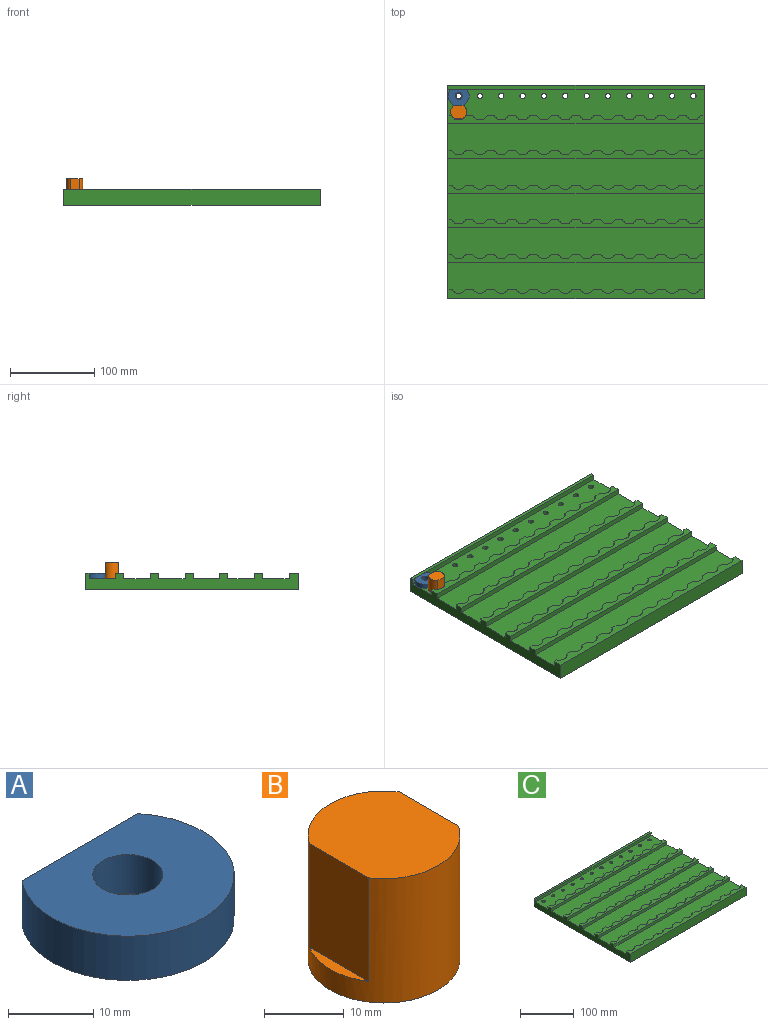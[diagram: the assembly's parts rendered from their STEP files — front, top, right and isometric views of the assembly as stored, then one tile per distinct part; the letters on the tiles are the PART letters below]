
ASSEMBLY  parts=3 mates=1
PART A: 7 faces, bbox 24.9x20.4x6.4 mm
  f0: plane 24.89x20.37mm, normal (0,0,-1), area 379.2mm2, adj f1,f2,f3
  f1: cylinder r=3.87mm len=7.75mm, axis (0,0,1), area 18.5mm2, adj f0,f4
  f2: cylinder r=12.45mm len=24.89mm, axis (0,0,-1), area 357.4mm2, adj f0,f3,f5
  f3: plane 19.19x6.35mm, normal (0,1,0), area 121.9mm2, adj f0,f2,f5
  f4: plane 8.2x8.2mm, normal (0,0,1), area 5.7mm2, adj f1,f6
  f5: plane 24.89x20.37mm, normal (0,0,1), area 373.4mm2, adj f2,f3,f6
  f6: cylinder r=4.1mm len=8.2mm, axis (0,0,1), area 144mm2, adj f4,f5
PART B: 7 faces, bbox 19.1x19.1x19.1 mm
  f0: cylinder r=9.53mm len=19.05mm, axis (0,0,-1), area 785.8mm2, adj f1,f2,f3,f4,f5,f6
  f1: plane 19.05x15.88mm, normal (0,0,1), area 262.3mm2, adj f0,f4,f6
  f2: plane 19.05x19.05mm, normal (0,0,-1), area 285mm2, adj f0
  f3: plane 10.53x1.59mm, normal (0,0,1), area 11.3mm2, adj f0,f4
  f4: plane 15.88x10.53mm, normal (1,0,0), area 167.2mm2, adj f0,f1,f3
  f5: plane 10.53x1.59mm, normal (0,0,1), area 11.3mm2, adj f0,f6
  f6: plane 15.88x10.53mm, normal (-1,0,0), area 167.2mm2, adj f0,f1,f5
PART C: 186 faces, bbox 304.8x254x19.1 mm
  f0: plane 254x19.05mm, normal (-1,0,0), area 3629mm2, adj f1,f2,f3,f4,f5,f6,f19,f20
  f1: plane 304.8x9.53mm, normal (0,0,1), area 2171mm2, adj f0,f21,f132,f133,f134,f135,f136,f137
  f2: plane 304.8x9.53mm, normal (0,0,1), area 2171mm2, adj f0,f21,f105,f106,f107,f108,f109,f110
  f3: plane 304.8x9.53mm, normal (0,0,1), area 2171mm2, adj f0,f21,f78,f79,f80,f81,f82,f83
  f4: plane 304.8x9.53mm, normal (0,0,1), area 2171mm2, adj f0,f21,f51,f52,f53,f54,f55,f56
  f5: plane 304.8x9.53mm, normal (0,0,1), area 2171mm2, adj f0,f21,f25,f26,f27,f28,f29,f30
  f6: plane 304.8x4.45mm, normal (0,0,1), area 1354.8mm2, adj f0,f19,f21,f45
  f7: cylinder r=3.17mm len=12.7mm, axis (0,0,1), area 253.4mm2, adj f22,f24
  f8: cylinder r=3.17mm len=12.7mm, axis (0,0,1), area 253.4mm2, adj f22,f24
  f9: cylinder r=3.17mm len=12.7mm, axis (0,0,1), area 253.4mm2, adj f22,f24
  f10: cylinder r=3.17mm len=12.7mm, axis (0,0,1), area 253.4mm2, adj f22,f24
  f11: cylinder r=3.17mm len=12.7mm, axis (0,0,1), area 253.4mm2, adj f22,f24
  f12: cylinder r=3.17mm len=12.7mm, axis (0,0,1), area 253.4mm2, adj f22,f24
  f13: cylinder r=3.17mm len=12.7mm, axis (0,0,1), area 253.4mm2, adj f22,f24
  f14: cylinder r=3.17mm len=12.7mm, axis (0,0,1), area 253.4mm2, adj f22,f24
  f15: cylinder r=3.17mm len=12.7mm, axis (0,0,1), area 253.4mm2, adj f22,f24
  f16: cylinder r=3.17mm len=12.7mm, axis (0,0,1), area 253.4mm2, adj f22,f24
  f17: cylinder r=3.17mm len=12.7mm, axis (0,0,1), area 253.4mm2, adj f22,f24
  f18: cylinder r=3.17mm len=12.7mm, axis (0,0,1), area 253.4mm2, adj f22,f24
  f19: plane 304.8x19.05mm, normal (0,1,0), area 5806.4mm2, adj f0,f6,f21,f22
  f20: plane 304.8x19.05mm, normal (0,-1,0), area 5806.4mm2, adj f0,f21,f22,f23
  f21: plane 254x19.05mm, normal (1,0,0), area 3629mm2, adj f1,f2,f3,f4,f5,f6,f19,f20
  f22: plane 304.8x254mm, normal (0,0,-1), area 77039.2mm2, adj f0,f7,f8,f9,f10,f11,f12,f13
  f23: plane 304.8x11.43mm, normal (0,0,1), area 2751.7mm2, adj f0,f20,f21,f159,f160,f161,f162,f163
  f24: plane 304.8x36.83mm, normal (0,0,1), area 10029.6mm2, adj f0,f7,f8,f9,f10,f11,f12,f13
  f25: cylinder r=9.53mm len=16.85mm, axis (0,0,1), area 131.3mm2, adj f5,f24,f26,f50
  f26: plane 8.55x6.35mm, normal (0,1,0), area 54.3mm2, adj f5,f24,f25,f27
  f27: cylinder r=9.53mm len=16.85mm, axis (0,0,1), area 131.3mm2, adj f5,f24,f26,f28
  f28: plane 8.55x6.35mm, normal (0,1,0), area 54.3mm2, adj f5,f24,f27,f29
  f29: cylinder r=9.53mm len=16.85mm, axis (0,0,1), area 131.3mm2, adj f5,f24,f28,f30
  f30: plane 8.55x6.35mm, normal (0,1,0), area 54.3mm2, adj f5,f24,f29,f31
  f31: cylinder r=9.53mm len=16.85mm, axis (0,0,1), area 131.3mm2, adj f5,f24,f30,f32
  f32: plane 8.55x6.35mm, normal (0,1,0), area 54.3mm2, adj f5,f24,f31,f33
  f33: cylinder r=9.53mm len=16.85mm, axis (0,0,1), area 131.3mm2, adj f5,f24,f32,f34
  f34: plane 8.55x6.35mm, normal (0,1,0), area 54.3mm2, adj f5,f24,f33,f35
  f35: cylinder r=9.53mm len=16.85mm, axis (0,0,1), area 131.3mm2, adj f5,f24,f34,f36
  f36: plane 8.55x6.35mm, normal (0,1,0), area 54.3mm2, adj f5,f24,f35,f37
  f37: cylinder r=9.53mm len=16.85mm, axis (0,0,1), area 131.3mm2, adj f5,f24,f36,f38
  f38: plane 8.55x6.35mm, normal (0,1,0), area 54.3mm2, adj f5,f24,f37,f39
  f39: cylinder r=9.53mm len=16.85mm, axis (0,0,1), area 131.3mm2, adj f5,f24,f38,f40
  f40: plane 8.55x6.35mm, normal (0,1,0), area 54.3mm2, adj f5,f24,f39,f41
  f41: cylinder r=9.53mm len=16.85mm, axis (0,0,1), area 131.3mm2, adj f5,f24,f40,f42
  f42: plane 8.55x6.35mm, normal (0,1,0), area 54.3mm2, adj f5,f24,f41,f43
  f43: cylinder r=9.53mm len=16.85mm, axis (0,0,1), area 131.3mm2, adj f5,f24,f42,f44
  f44: plane 6.35x4.28mm, normal (0,1,0), area 27.2mm2, adj f5,f21,f24,f43
  f45: plane 304.8x6.35mm, normal (0,-1,0), area 1935.5mm2, adj f0,f6,f21,f24
  f46: plane 6.35x4.28mm, normal (0,1,0), area 27.2mm2, adj f0,f5,f24,f47
  f47: cylinder r=9.53mm len=16.85mm, axis (0,0,1), area 131.3mm2, adj f5,f24,f46,f48
  f48: plane 8.55x6.35mm, normal (0,1,0), area 54.3mm2, adj f5,f24,f47,f49
  f49: cylinder r=9.53mm len=16.85mm, axis (0,0,1), area 131.3mm2, adj f5,f24,f48,f50
  f50: plane 8.55x6.35mm, normal (0,1,0), area 54.3mm2, adj f5,f24,f25,f49
  f51: cylinder r=9.53mm len=16.85mm, axis (0,0,1), area 131.3mm2, adj f4,f52,f76,f77
  f52: plane 8.55x6.35mm, normal (0,1,0), area 54.3mm2, adj f4,f51,f53,f77
  f53: cylinder r=9.53mm len=16.85mm, axis (0,0,1), area 131.3mm2, adj f4,f52,f54,f77
  f54: plane 8.55x6.35mm, normal (0,1,0), area 54.3mm2, adj f4,f53,f55,f77
  f55: cylinder r=9.53mm len=16.85mm, axis (0,0,1), area 131.3mm2, adj f4,f54,f56,f77
  f56: plane 8.55x6.35mm, normal (0,1,0), area 54.3mm2, adj f4,f55,f57,f77
  f57: cylinder r=9.53mm len=16.85mm, axis (0,0,1), area 131.3mm2, adj f4,f56,f58,f77
  f58: plane 8.55x6.35mm, normal (0,1,0), area 54.3mm2, adj f4,f57,f59,f77
  f59: cylinder r=9.53mm len=16.85mm, axis (0,0,1), area 131.3mm2, adj f4,f58,f60,f77
  f60: plane 8.55x6.35mm, normal (0,1,0), area 54.3mm2, adj f4,f59,f61,f77
  f61: cylinder r=9.53mm len=16.85mm, axis (0,0,1), area 131.3mm2, adj f4,f60,f62,f77
  f62: plane 8.55x6.35mm, normal (0,1,0), area 54.3mm2, adj f4,f61,f63,f77
  f63: cylinder r=9.53mm len=16.85mm, axis (0,0,1), area 131.3mm2, adj f4,f62,f64,f77
  f64: plane 8.55x6.35mm, normal (0,1,0), area 54.3mm2, adj f4,f63,f65,f77
  f65: cylinder r=9.53mm len=16.85mm, axis (0,0,1), area 131.3mm2, adj f4,f64,f66,f77
  f66: plane 8.55x6.35mm, normal (0,1,0), area 54.3mm2, adj f4,f65,f67,f77
  f67: cylinder r=9.53mm len=16.85mm, axis (0,0,1), area 131.3mm2, adj f4,f66,f68,f77
  f68: plane 8.55x6.35mm, normal (0,1,0), area 54.3mm2, adj f4,f67,f69,f77
  f69: cylinder r=9.53mm len=16.85mm, axis (0,0,1), area 131.3mm2, adj f4,f68,f70,f77
  f70: plane 6.35x4.28mm, normal (0,1,0), area 27.2mm2, adj f4,f21,f69,f77
  f71: plane 304.8x6.35mm, normal (0,-1,0), area 1935.5mm2, adj f0,f5,f21,f77
  f72: plane 6.35x4.28mm, normal (0,1,0), area 27.2mm2, adj f0,f4,f73,f77
  f73: cylinder r=9.53mm len=16.85mm, axis (0,0,1), area 131.3mm2, adj f4,f72,f74,f77
  f74: plane 8.55x6.35mm, normal (0,1,0), area 54.3mm2, adj f4,f73,f75,f77
  f75: cylinder r=9.53mm len=16.85mm, axis (0,0,1), area 131.3mm2, adj f4,f74,f76,f77
  f76: plane 8.55x6.35mm, normal (0,1,0), area 54.3mm2, adj f4,f51,f75,f77
  f77: plane 304.8x36.83mm, normal (0,0,1), area 10409.6mm2, adj f0,f21,f51,f52,f53,f54,f55,f56
  f78: cylinder r=9.53mm len=16.85mm, axis (0,0,1), area 131.3mm2, adj f3,f79,f103,f104
  f79: plane 8.55x6.35mm, normal (0,1,0), area 54.3mm2, adj f3,f78,f80,f104
  f80: cylinder r=9.53mm len=16.85mm, axis (0,0,1), area 131.3mm2, adj f3,f79,f81,f104
  f81: plane 8.55x6.35mm, normal (0,1,0), area 54.3mm2, adj f3,f80,f82,f104
  f82: cylinder r=9.53mm len=16.85mm, axis (0,0,1), area 131.3mm2, adj f3,f81,f83,f104
  f83: plane 8.55x6.35mm, normal (0,1,0), area 54.3mm2, adj f3,f82,f84,f104
  f84: cylinder r=9.53mm len=16.85mm, axis (0,0,1), area 131.3mm2, adj f3,f83,f85,f104
  f85: plane 8.55x6.35mm, normal (0,1,0), area 54.3mm2, adj f3,f84,f86,f104
  f86: cylinder r=9.53mm len=16.85mm, axis (0,0,1), area 131.3mm2, adj f3,f85,f87,f104
  f87: plane 8.55x6.35mm, normal (0,1,0), area 54.3mm2, adj f3,f86,f88,f104
  f88: cylinder r=9.53mm len=16.85mm, axis (0,0,1), area 131.3mm2, adj f3,f87,f89,f104
  f89: plane 8.55x6.35mm, normal (0,1,0), area 54.3mm2, adj f3,f88,f90,f104
  f90: cylinder r=9.53mm len=16.85mm, axis (0,0,1), area 131.3mm2, adj f3,f89,f91,f104
  f91: plane 8.55x6.35mm, normal (0,1,0), area 54.3mm2, adj f3,f90,f92,f104
  f92: cylinder r=9.53mm len=16.85mm, axis (0,0,1), area 131.3mm2, adj f3,f91,f93,f104
  f93: plane 8.55x6.35mm, normal (0,1,0), area 54.3mm2, adj f3,f92,f94,f104
  f94: cylinder r=9.53mm len=16.85mm, axis (0,0,1), area 131.3mm2, adj f3,f93,f95,f104
  f95: plane 8.55x6.35mm, normal (0,1,0), area 54.3mm2, adj f3,f94,f96,f104
  f96: cylinder r=9.53mm len=16.85mm, axis (0,0,1), area 131.3mm2, adj f3,f95,f97,f104
  f97: plane 6.35x4.28mm, normal (0,1,0), area 27.2mm2, adj f3,f21,f96,f104
  f98: plane 304.8x6.35mm, normal (0,-1,0), area 1935.5mm2, adj f0,f4,f21,f104
  f99: plane 6.35x4.28mm, normal (0,1,0), area 27.2mm2, adj f0,f3,f100,f104
  f100: cylinder r=9.53mm len=16.85mm, axis (0,0,1), area 131.3mm2, adj f3,f99,f101,f104
  f101: plane 8.55x6.35mm, normal (0,1,0), area 54.3mm2, adj f3,f100,f102,f104
  f102: cylinder r=9.53mm len=16.85mm, axis (0,0,1), area 131.3mm2, adj f3,f101,f103,f104
  f103: plane 8.55x6.35mm, normal (0,1,0), area 54.3mm2, adj f3,f78,f102,f104
  f104: plane 304.8x36.83mm, normal (0,0,1), area 10409.6mm2, adj f0,f21,f78,f79,f80,f81,f82,f83
  f105: cylinder r=9.53mm len=16.85mm, axis (0,0,1), area 131.3mm2, adj f2,f106,f130,f131
  f106: plane 8.55x6.35mm, normal (0,1,0), area 54.3mm2, adj f2,f105,f107,f131
  f107: cylinder r=9.53mm len=16.85mm, axis (0,0,1), area 131.3mm2, adj f2,f106,f108,f131
  f108: plane 8.55x6.35mm, normal (0,1,0), area 54.3mm2, adj f2,f107,f109,f131
  f109: cylinder r=9.53mm len=16.85mm, axis (0,0,1), area 131.3mm2, adj f2,f108,f110,f131
  f110: plane 8.55x6.35mm, normal (0,1,0), area 54.3mm2, adj f2,f109,f111,f131
  f111: cylinder r=9.53mm len=16.85mm, axis (0,0,1), area 131.3mm2, adj f2,f110,f112,f131
  f112: plane 8.55x6.35mm, normal (0,1,0), area 54.3mm2, adj f2,f111,f113,f131
  f113: cylinder r=9.53mm len=16.85mm, axis (0,0,1), area 131.3mm2, adj f2,f112,f114,f131
  f114: plane 8.55x6.35mm, normal (0,1,0), area 54.3mm2, adj f2,f113,f115,f131
  f115: cylinder r=9.53mm len=16.85mm, axis (0,0,1), area 131.3mm2, adj f2,f114,f116,f131
  f116: plane 8.55x6.35mm, normal (0,1,0), area 54.3mm2, adj f2,f115,f117,f131
  f117: cylinder r=9.53mm len=16.85mm, axis (0,0,1), area 131.3mm2, adj f2,f116,f118,f131
  f118: plane 8.55x6.35mm, normal (0,1,0), area 54.3mm2, adj f2,f117,f119,f131
  f119: cylinder r=9.53mm len=16.85mm, axis (0,0,1), area 131.3mm2, adj f2,f118,f120,f131
  f120: plane 8.55x6.35mm, normal (0,1,0), area 54.3mm2, adj f2,f119,f121,f131
  f121: cylinder r=9.53mm len=16.85mm, axis (0,0,1), area 131.3mm2, adj f2,f120,f122,f131
  f122: plane 8.55x6.35mm, normal (0,1,0), area 54.3mm2, adj f2,f121,f123,f131
  f123: cylinder r=9.53mm len=16.85mm, axis (0,0,1), area 131.3mm2, adj f2,f122,f124,f131
  f124: plane 6.35x4.28mm, normal (0,1,0), area 27.2mm2, adj f2,f21,f123,f131
  f125: plane 304.8x6.35mm, normal (0,-1,0), area 1935.5mm2, adj f0,f3,f21,f131
  f126: plane 6.35x4.28mm, normal (0,1,0), area 27.2mm2, adj f0,f2,f127,f131
  f127: cylinder r=9.53mm len=16.85mm, axis (0,0,1), area 131.3mm2, adj f2,f126,f128,f131
  f128: plane 8.55x6.35mm, normal (0,1,0), area 54.3mm2, adj f2,f127,f129,f131
  f129: cylinder r=9.53mm len=16.85mm, axis (0,0,1), area 131.3mm2, adj f2,f128,f130,f131
  f130: plane 8.55x6.35mm, normal (0,1,0), area 54.3mm2, adj f2,f105,f129,f131
  f131: plane 304.8x36.83mm, normal (0,0,1), area 10409.6mm2, adj f0,f21,f105,f106,f107,f108,f109,f110
  f132: cylinder r=9.53mm len=16.85mm, axis (0,0,1), area 131.3mm2, adj f1,f133,f157,f158
  f133: plane 8.55x6.35mm, normal (0,1,0), area 54.3mm2, adj f1,f132,f134,f158
  f134: cylinder r=9.53mm len=16.85mm, axis (0,0,1), area 131.3mm2, adj f1,f133,f135,f158
  f135: plane 8.55x6.35mm, normal (0,1,0), area 54.3mm2, adj f1,f134,f136,f158
  f136: cylinder r=9.53mm len=16.85mm, axis (0,0,1), area 131.3mm2, adj f1,f135,f137,f158
  f137: plane 8.55x6.35mm, normal (0,1,0), area 54.3mm2, adj f1,f136,f138,f158
  f138: cylinder r=9.53mm len=16.85mm, axis (0,0,1), area 131.3mm2, adj f1,f137,f139,f158
  f139: plane 8.55x6.35mm, normal (0,1,0), area 54.3mm2, adj f1,f138,f140,f158
  f140: cylinder r=9.53mm len=16.85mm, axis (0,0,1), area 131.3mm2, adj f1,f139,f141,f158
  f141: plane 8.55x6.35mm, normal (0,1,0), area 54.3mm2, adj f1,f140,f142,f158
  f142: cylinder r=9.53mm len=16.85mm, axis (0,0,1), area 131.3mm2, adj f1,f141,f143,f158
  f143: plane 8.55x6.35mm, normal (0,1,0), area 54.3mm2, adj f1,f142,f144,f158
  f144: cylinder r=9.53mm len=16.85mm, axis (0,0,1), area 131.3mm2, adj f1,f143,f145,f158
  f145: plane 8.55x6.35mm, normal (0,1,0), area 54.3mm2, adj f1,f144,f146,f158
  f146: cylinder r=9.53mm len=16.85mm, axis (0,0,1), area 131.3mm2, adj f1,f145,f147,f158
  f147: plane 8.55x6.35mm, normal (0,1,0), area 54.3mm2, adj f1,f146,f148,f158
  f148: cylinder r=9.53mm len=16.85mm, axis (0,0,1), area 131.3mm2, adj f1,f147,f149,f158
  f149: plane 8.55x6.35mm, normal (0,1,0), area 54.3mm2, adj f1,f148,f150,f158
  f150: cylinder r=9.53mm len=16.85mm, axis (0,0,1), area 131.3mm2, adj f1,f149,f151,f158
  f151: plane 6.35x4.28mm, normal (0,1,0), area 27.2mm2, adj f1,f21,f150,f158
  f152: plane 304.8x6.35mm, normal (0,-1,0), area 1935.5mm2, adj f0,f2,f21,f158
  f153: plane 6.35x4.28mm, normal (0,1,0), area 27.2mm2, adj f0,f1,f154,f158
  f154: cylinder r=9.53mm len=16.85mm, axis (0,0,1), area 131.3mm2, adj f1,f153,f155,f158
  f155: plane 8.55x6.35mm, normal (0,1,0), area 54.3mm2, adj f1,f154,f156,f158
  f156: cylinder r=9.53mm len=16.85mm, axis (0,0,1), area 131.3mm2, adj f1,f155,f157,f158
  f157: plane 8.55x6.35mm, normal (0,1,0), area 54.3mm2, adj f1,f132,f156,f158
  f158: plane 304.8x36.83mm, normal (0,0,1), area 10409.6mm2, adj f0,f21,f132,f133,f134,f135,f136,f137
  f159: cylinder r=9.53mm len=16.85mm, axis (0,0,1), area 131.3mm2, adj f23,f160,f184,f185
  f160: plane 8.55x6.35mm, normal (0,1,0), area 54.3mm2, adj f23,f159,f161,f185
  f161: cylinder r=9.53mm len=16.85mm, axis (0,0,1), area 131.3mm2, adj f23,f160,f162,f185
  f162: plane 8.55x6.35mm, normal (0,1,0), area 54.3mm2, adj f23,f161,f163,f185
  f163: cylinder r=9.53mm len=16.85mm, axis (0,0,1), area 131.3mm2, adj f23,f162,f164,f185
  f164: plane 8.55x6.35mm, normal (0,1,0), area 54.3mm2, adj f23,f163,f165,f185
  f165: cylinder r=9.53mm len=16.85mm, axis (0,0,1), area 131.3mm2, adj f23,f164,f166,f185
  f166: plane 8.55x6.35mm, normal (0,1,0), area 54.3mm2, adj f23,f165,f167,f185
  f167: cylinder r=9.53mm len=16.85mm, axis (0,0,1), area 131.3mm2, adj f23,f166,f168,f185
  f168: plane 8.55x6.35mm, normal (0,1,0), area 54.3mm2, adj f23,f167,f169,f185
  f169: cylinder r=9.53mm len=16.85mm, axis (0,0,1), area 131.3mm2, adj f23,f168,f170,f185
  f170: plane 8.55x6.35mm, normal (0,1,0), area 54.3mm2, adj f23,f169,f171,f185
  f171: cylinder r=9.53mm len=16.85mm, axis (0,0,1), area 131.3mm2, adj f23,f170,f172,f185
  f172: plane 8.55x6.35mm, normal (0,1,0), area 54.3mm2, adj f23,f171,f173,f185
  f173: cylinder r=9.53mm len=16.85mm, axis (0,0,1), area 131.3mm2, adj f23,f172,f174,f185
  f174: plane 8.55x6.35mm, normal (0,1,0), area 54.3mm2, adj f23,f173,f175,f185
  f175: cylinder r=9.53mm len=16.85mm, axis (0,0,1), area 131.3mm2, adj f23,f174,f176,f185
  f176: plane 8.55x6.35mm, normal (0,1,0), area 54.3mm2, adj f23,f175,f177,f185
  f177: cylinder r=9.53mm len=16.85mm, axis (0,0,1), area 131.3mm2, adj f23,f176,f178,f185
  f178: plane 6.35x4.28mm, normal (0,1,0), area 27.2mm2, adj f21,f23,f177,f185
  f179: plane 304.8x6.35mm, normal (0,-1,0), area 1935.5mm2, adj f0,f1,f21,f185
  f180: plane 6.35x4.28mm, normal (0,1,0), area 27.2mm2, adj f0,f23,f181,f185
  f181: cylinder r=9.53mm len=16.85mm, axis (0,0,1), area 131.3mm2, adj f23,f180,f182,f185
  f182: plane 8.55x6.35mm, normal (0,1,0), area 54.3mm2, adj f23,f181,f183,f185
  f183: cylinder r=9.53mm len=16.85mm, axis (0,0,1), area 131.3mm2, adj f23,f182,f184,f185
  f184: plane 8.55x6.35mm, normal (0,1,0), area 54.3mm2, adj f23,f159,f183,f185
  f185: plane 304.8x36.83mm, normal (0,0,1), area 10409.6mm2, adj f0,f21,f159,f160,f161,f162,f163,f164
PLACE A t=(-139.7,-10.48,-6.35)mm
PLACE B rot(axis=(0,0,1),90deg) t=(-139.3,-29.39,-6.33)mm
PLACE C t=(-152.4,2.22,0)mm
MATE fastened A.f1 <-> C.f18  axis (0,0,-1) through (-139.7,-10.48,-6.35)mm
